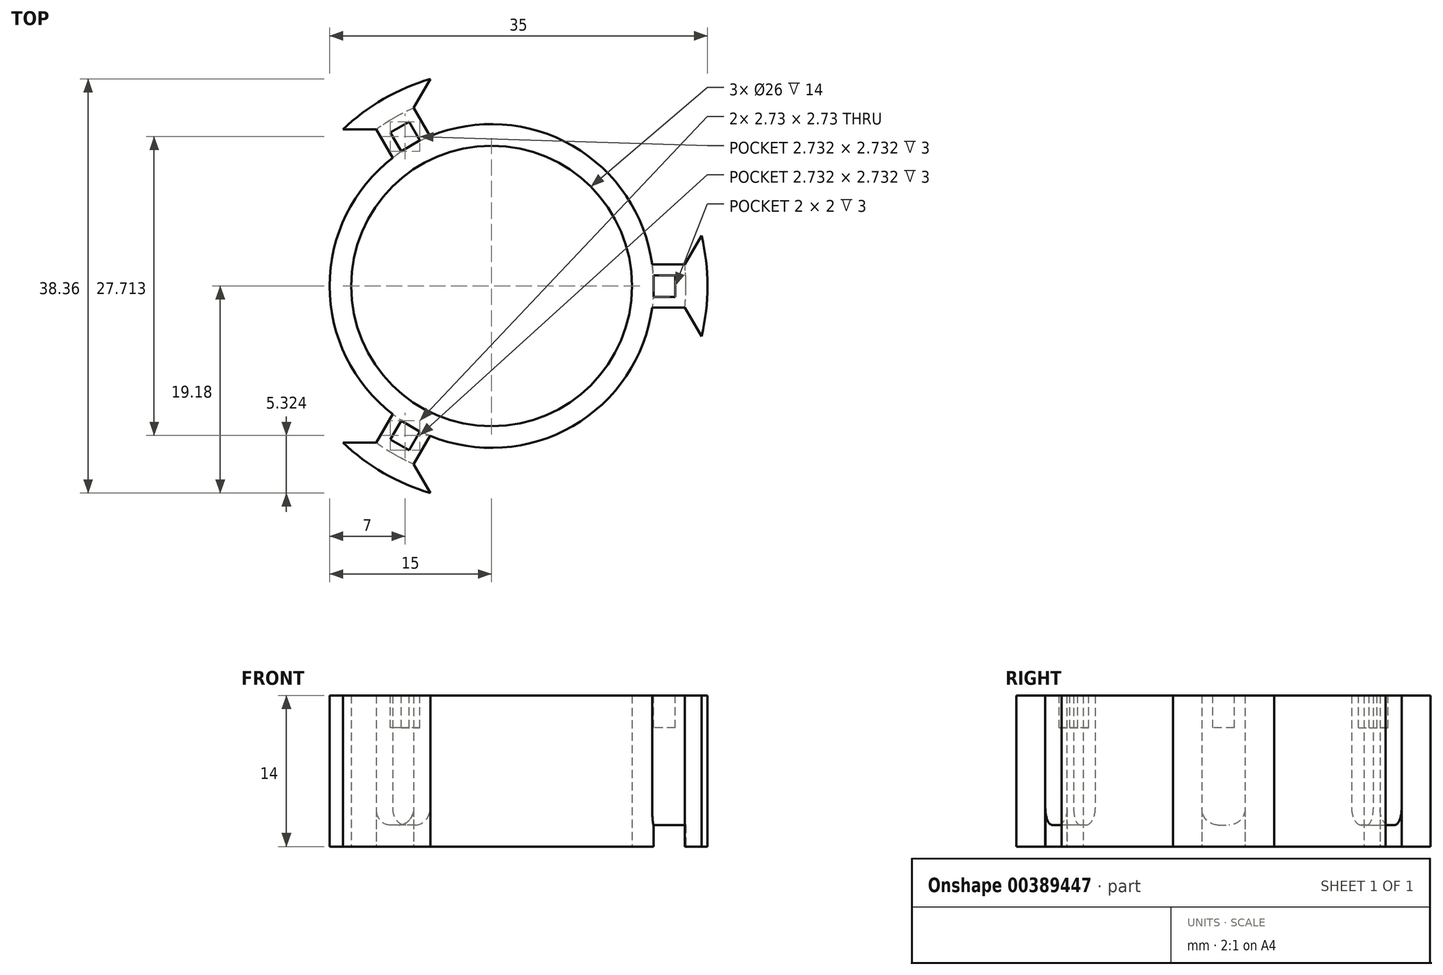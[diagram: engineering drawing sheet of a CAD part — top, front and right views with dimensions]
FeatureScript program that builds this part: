
annotation { "Feature Type Name" : "Feature", "Feature Type Description" : "" }
export const myFeature = defineFeature(function(context is Context, id is Id, definition is map)
    precondition{}
    {
        {
            var Q0;
            Q0=qCreatedBy(makeId("Top.planeOp"),FACE);
            var sketch = newSketch(context, id + "F0", { "sketchPlane" : qUnion([Q0])});
            skCircle(sketch, "E0", {"center": v(0, 0) * mm, "radius": 13 * mm});
            skCircle(sketch, "E1", {"center": v(0, 0) * mm, "radius": 15 * mm});
            skPoint(sketch, "E2.end.orphan", {"position": v(0, 21.28) * mm});
            skLineSegment(sketch, "E3", {"start": v(0, 0) * mm, "end": v(20, 0) * mm});
            skLineSegment(sketch, "E4", {"start": v(20, 0) * mm, "end": v(0, 0) * mm});
            skLineSegment(sketch, "E5", {"start": v(-10, -17.32) * mm, "end": v(0, 0) * mm});
            skLineSegment(sketch, "E6", {"start": v(0, 0) * mm, "end": v(-10, 17.32) * mm});
            skLineSegment(sketch, "E7", {"start": v(-9.17, 11.87) * mm, "end": v(-11.68, 16.23) * mm});
            skLineSegment(sketch, "E8", {"start": v(-5.7, 13.87) * mm, "end": v(-8.21, 18.22) * mm});
            skLineSegment(sketch, "E9", {"start": v(-11.73, 16.32) * mm, "end": v(-11.74, 16.31) * mm});
            skArc(sketch, "E10", {"start": v(-5.67, 19.18) * mm, "mid": v(-10, 17.32) * mm, "end": v(-13.77, 14.5) * mm});
            skLineSegment(sketch, "E11", {"start": v(-10.68, 14.5) * mm, "end": v(-13.77, 14.5) * mm});
            skLineSegment(sketch, "E12", {"start": v(-5.67, 19.18) * mm, "end": v(-7.22, 16.5) * mm});
            skPoint(sketch, "E13.orphan", {"position": v(-8.22, 18.23) * mm});
            skLineSegment(sketch, "E14.1.0", {"start": v(-9.17, -11.87) * mm, "end": v(-11.68, -16.22) * mm});
            skLineSegment(sketch, "E14.1.1", {"start": v(-13.77, -14.5) * mm, "end": v(-10.68, -14.5) * mm});
            skArc(sketch, "E14.1.2", {"start": v(-13.77, -14.5) * mm, "mid": v(-10, -17.32) * mm, "end": v(-5.67, -19.18) * mm});
            skLineSegment(sketch, "E14.1.3", {"start": v(-7.22, -16.5) * mm, "end": v(-5.67, -19.18) * mm});
            skLineSegment(sketch, "E14.1.4", {"start": v(-5.7, -13.87) * mm, "end": v(-8.22, -18.23) * mm});
            skLineSegment(sketch, "E14.2.0", {"start": v(14.87, -2) * mm, "end": v(19.89, -2) * mm});
            skLineSegment(sketch, "E14.2.1", {"start": v(19.45, -4.68) * mm, "end": v(17.9, -2) * mm});
            skArc(sketch, "E14.2.2", {"start": v(19.45, -4.68) * mm, "mid": v(20, 0) * mm, "end": v(19.45, 4.68) * mm});
            skLineSegment(sketch, "E14.2.3", {"start": v(17.9, 2) * mm, "end": v(19.45, 4.68) * mm});
            skLineSegment(sketch, "E14.2.4", {"start": v(14.87, 2) * mm, "end": v(19.9, 2) * mm});
            skSolve(sketch);
        }
        {
            var Q0;
            Q0=qSketchRegion(id+"F0",true);
            extrude(context, id + "F1", {"entities" : qUnion([Q0]), "depth" : 28 * mm});
        }
        {
            var Q0;
            Q0=qCreatedBy(makeId("Top.planeOp"),FACE);
            var sketch = newSketch(context, id + "F2", { "sketchPlane" : qUnion([Q0])});
            skCircle(sketch, "E15", {"center": v(0, 0) * mm, "radius": 15 * mm});
            skCircle(sketch, "E16", {"center": v(0, 0) * mm, "radius": 18 * mm});
            skSolve(sketch);
        }
        {
            var Q0;
            Q0=makeQuery(id+"F2.imprint","IMPRINT",FACE,{"disambiguationData":[TD([[makeQuery(id+"F2.imprint","IMPRINT",EDGE,{"derivedFrom":sQuery(id+"F2.wireOp",EDGE,"E15")}),-1.0]])]});
            extrude(context, id + "F3", {"entities" : qUnion([Q0]), "operationType" : NewBodyOperationType.REMOVE, "depth" : 2 * mm});
        }
        {
            var Q0;
            Q0=makeQuery(id+"F1.opExtrude","CAP_FACE",FACE,{"disambiguationData":[OSD([sQuery(id+"F0.wireOp",EDGE,"E0"),sQuery(id+"F0.wireOp",EDGE,"E1"),sQuery(id+"F0.wireOp",EDGE,"E7"),sQuery(id+"F0.wireOp",EDGE,"E8"),sQuery(id+"F0.wireOp",EDGE,"E10"),sQuery(id+"F0.wireOp",EDGE,"E11"),sQuery(id+"F0.wireOp",EDGE,"E12"),sQuery(id+"F0.wireOp",EDGE,"E14.1.0"),sQuery(id+"F0.wireOp",EDGE,"E14.1.1"),sQuery(id+"F0.wireOp",EDGE,"E14.1.2"),sQuery(id+"F0.wireOp",EDGE,"E14.1.3"),sQuery(id+"F0.wireOp",EDGE,"E14.1.4"),sQuery(id+"F0.wireOp",EDGE,"E14.2.0"),sQuery(id+"F0.wireOp",EDGE,"E14.2.1"),sQuery(id+"F0.wireOp",EDGE,"E14.2.2"),sQuery(id+"F0.wireOp",EDGE,"E14.2.3"),sQuery(id+"F0.wireOp",EDGE,"E14.2.4")])],"isStart":false});
            var sketch = newSketch(context, id + "F4", { "sketchPlane" : qUnion([Q0])});
            skCircle(sketch, "E17", {"center": v(0, 0) * mm, "radius": 15 * mm});
            skCircle(sketch, "E18", {"center": v(0, 0) * mm, "radius": 18.01 * mm});
            skSolve(sketch);
        }
        {
            var Q0;
            Q0=qSketchRegion(id+"F4",true);
            extrude(context, id + "F5", {"entities" : qUnion([Q0]), "operationType" : NewBodyOperationType.REMOVE, "oppositeDirection" : true, "depth" : 2 * mm});
        }
        {
            var Q0;
            Q0=makeQuery(id+"F5.boolean.opBoolean","INTERSECT",EDGE,{"derivedFrom":[makeQuery(id+"F1.opExtrude","SWEPT_FACE",FACE,{"disambiguationData":[OSD([sQuery(id+"F0.wireOp",EDGE,"E14.1.4")])]}),makeQuery(id+"F5.opExtrude","CAP_FACE",FACE,{"disambiguationData":[OSD([sQuery(id+"F4.wireOp",EDGE,"E17"),sQuery(id+"F4.wireOp",EDGE,"E18")])],"isStart":false})]});
            var Q1;
            Q1=makeQuery(id+"F5.boolean.opBoolean","INTERSECT",EDGE,{"derivedFrom":[makeQuery(id+"F1.opExtrude","SWEPT_FACE",FACE,{"disambiguationData":[OSD([sQuery(id+"F0.wireOp",EDGE,"E14.1.0")])]}),makeQuery(id+"F5.opExtrude","CAP_FACE",FACE,{"disambiguationData":[OSD([sQuery(id+"F4.wireOp",EDGE,"E17"),sQuery(id+"F4.wireOp",EDGE,"E18")])],"isStart":false})]});
            var Q2;
            Q2=makeQuery(id+"F5.boolean.opBoolean","INTERSECT",EDGE,{"derivedFrom":[makeQuery(id+"F1.opExtrude","SWEPT_FACE",FACE,{"disambiguationData":[OSD([sQuery(id+"F0.wireOp",EDGE,"E14.2.0")])]}),makeQuery(id+"F5.opExtrude","CAP_FACE",FACE,{"disambiguationData":[OSD([sQuery(id+"F4.wireOp",EDGE,"E17"),sQuery(id+"F4.wireOp",EDGE,"E18")])],"isStart":false})]});
            var Q3;
            Q3=makeQuery(id+"F5.boolean.opBoolean","INTERSECT",EDGE,{"derivedFrom":[makeQuery(id+"F1.opExtrude","SWEPT_FACE",FACE,{"disambiguationData":[OSD([sQuery(id+"F0.wireOp",EDGE,"E14.2.4")])]}),makeQuery(id+"F5.opExtrude","CAP_FACE",FACE,{"disambiguationData":[OSD([sQuery(id+"F4.wireOp",EDGE,"E17"),sQuery(id+"F4.wireOp",EDGE,"E18")])],"isStart":false})]});
            var Q4;
            Q4=makeQuery(id+"F5.boolean.opBoolean","INTERSECT",EDGE,{"derivedFrom":[makeQuery(id+"F1.opExtrude","SWEPT_FACE",FACE,{"disambiguationData":[OSD([sQuery(id+"F0.wireOp",EDGE,"E8")])]}),makeQuery(id+"F5.opExtrude","CAP_FACE",FACE,{"disambiguationData":[OSD([sQuery(id+"F4.wireOp",EDGE,"E17"),sQuery(id+"F4.wireOp",EDGE,"E18")])],"isStart":false})]});
            var Q5;
            Q5=makeQuery(id+"F5.boolean.opBoolean","INTERSECT",EDGE,{"derivedFrom":[makeQuery(id+"F1.opExtrude","SWEPT_FACE",FACE,{"disambiguationData":[OSD([sQuery(id+"F0.wireOp",EDGE,"E7")])]}),makeQuery(id+"F5.opExtrude","CAP_FACE",FACE,{"disambiguationData":[OSD([sQuery(id+"F4.wireOp",EDGE,"E17"),sQuery(id+"F4.wireOp",EDGE,"E18")])],"isStart":false})]});
            var Q6;
            Q6=makeQuery(id+"F3.boolean.opBoolean","INTERSECT",EDGE,{"derivedFrom":[makeQuery(id+"F1.opExtrude","SWEPT_FACE",FACE,{"disambiguationData":[OSD([sQuery(id+"F0.wireOp",EDGE,"E7")])]}),makeQuery(id+"F3.opExtrude","CAP_FACE",FACE,{"disambiguationData":[OSD([sQuery(id+"F2.wireOp",EDGE,"E15"),sQuery(id+"F2.wireOp",EDGE,"E16")])],"isStart":false})]});
            var Q7;
            Q7=makeQuery(id+"F3.boolean.opBoolean","INTERSECT",EDGE,{"derivedFrom":[makeQuery(id+"F1.opExtrude","SWEPT_FACE",FACE,{"disambiguationData":[OSD([sQuery(id+"F0.wireOp",EDGE,"E8")])]}),makeQuery(id+"F3.opExtrude","CAP_FACE",FACE,{"disambiguationData":[OSD([sQuery(id+"F2.wireOp",EDGE,"E15"),sQuery(id+"F2.wireOp",EDGE,"E16")])],"isStart":false})]});
            var Q8;
            Q8=makeQuery(id+"F3.boolean.opBoolean","INTERSECT",EDGE,{"derivedFrom":[makeQuery(id+"F1.opExtrude","SWEPT_FACE",FACE,{"disambiguationData":[OSD([sQuery(id+"F0.wireOp",EDGE,"E14.2.4")])]}),makeQuery(id+"F3.opExtrude","CAP_FACE",FACE,{"disambiguationData":[OSD([sQuery(id+"F2.wireOp",EDGE,"E15"),sQuery(id+"F2.wireOp",EDGE,"E16")])],"isStart":false})]});
            var Q9;
            Q9=makeQuery(id+"F3.boolean.opBoolean","INTERSECT",EDGE,{"derivedFrom":[makeQuery(id+"F1.opExtrude","SWEPT_FACE",FACE,{"disambiguationData":[OSD([sQuery(id+"F0.wireOp",EDGE,"E14.2.0")])]}),makeQuery(id+"F3.opExtrude","CAP_FACE",FACE,{"disambiguationData":[OSD([sQuery(id+"F2.wireOp",EDGE,"E15"),sQuery(id+"F2.wireOp",EDGE,"E16")])],"isStart":false})]});
            var Q10;
            Q10=makeQuery(id+"F3.boolean.opBoolean","INTERSECT",EDGE,{"derivedFrom":[makeQuery(id+"F1.opExtrude","SWEPT_FACE",FACE,{"disambiguationData":[OSD([sQuery(id+"F0.wireOp",EDGE,"E14.1.0")])]}),makeQuery(id+"F3.opExtrude","CAP_FACE",FACE,{"disambiguationData":[OSD([sQuery(id+"F2.wireOp",EDGE,"E15"),sQuery(id+"F2.wireOp",EDGE,"E16")])],"isStart":false})]});
            var Q11;
            Q11=makeQuery(id+"F3.boolean.opBoolean","INTERSECT",EDGE,{"derivedFrom":[makeQuery(id+"F1.opExtrude","SWEPT_FACE",FACE,{"disambiguationData":[OSD([sQuery(id+"F0.wireOp",EDGE,"E14.1.4")])]}),makeQuery(id+"F3.opExtrude","CAP_FACE",FACE,{"disambiguationData":[OSD([sQuery(id+"F2.wireOp",EDGE,"E15"),sQuery(id+"F2.wireOp",EDGE,"E16")])],"isStart":false})]});
            fillet(context, id + "F6", {"entities" : qUnion([Q0, Q1, Q2, Q3, Q4, Q5, Q6, Q7, Q8, Q9, Q10, Q11]), "radius" : 1.5 * mm, "tangentPropagation" : true, "allowEdgeOverflow" : false});
        }
        {
            var Q0;
            {var subQ0=sQuery(id+"F0.wireOp",EDGE,"E14.1.1");var subQ1=sQuery(id+"F0.wireOp",EDGE,"E14.1.2");var subQ2=sQuery(id+"F0.wireOp",EDGE,"E14.1.3");Q0=makeQuery(id+"F5.boolean.opBoolean","SPLIT",FACE,{"disambiguationData":[TD([makeQuery(id+"F1.opExtrude","SWEPT_FACE",FACE,{"disambiguationData":[OSD([subQ0])]})])],"derivedFrom":makeQuery(id+"F1.opExtrude","CAP_FACE",FACE,{"disambiguationData":[OSD([sQuery(id+"F0.wireOp",EDGE,"E0"),sQuery(id+"F0.wireOp",EDGE,"E1"),sQuery(id+"F0.wireOp",EDGE,"E7"),sQuery(id+"F0.wireOp",EDGE,"E8"),sQuery(id+"F0.wireOp",EDGE,"E10"),sQuery(id+"F0.wireOp",EDGE,"E11"),sQuery(id+"F0.wireOp",EDGE,"E12"),sQuery(id+"F0.wireOp",EDGE,"E14.1.0"),subQ0,subQ1,subQ2,sQuery(id+"F0.wireOp",EDGE,"E14.1.4"),sQuery(id+"F0.wireOp",EDGE,"E14.2.0"),sQuery(id+"F0.wireOp",EDGE,"E14.2.1"),sQuery(id+"F0.wireOp",EDGE,"E14.2.2"),sQuery(id+"F0.wireOp",EDGE,"E14.2.3"),sQuery(id+"F0.wireOp",EDGE,"E14.2.4")])],"isStart":false})});}
            var sketch = newSketch(context, id + "F7", { "sketchPlane" : qUnion([Q0])});
            skCircle(sketch, "E19", {"center": v(0, 0) * mm, "radius": 25.29 * mm});
            skSolve(sketch);
        }
        {
            var Q0;
            Q0=qSketchRegion(id+"F7",true);
            extrude(context, id + "F8", {"entities" : qUnion([Q0]), "operationType" : NewBodyOperationType.REMOVE, "oppositeDirection" : true, "depth" : (28 / 2) * mm});
        }
        {
            var Q0;
            Q0=makeQuery(id+"F8.boolean.opBoolean","COPY",FACE,{"derivedFrom":makeQuery(id+"F8.opExtrude","CAP_FACE",FACE,{"disambiguationData":[OSD([sQuery(id+"F7.wireOp",EDGE,"E19")])],"isStart":false})});
            var sketch = newSketch(context, id + "F9", { "sketchPlane" : qUnion([Q0])});
            skLineSegment(sketch, "E20.bottom", {"start": v(17, 1) * mm, "end": v(15, 1) * mm});
            skLineSegment(sketch, "E20.top", {"start": v(17, -1) * mm, "end": v(15, -1) * mm});
            skLineSegment(sketch, "E20.left", {"start": v(17, 1) * mm, "end": v(17, -1) * mm});
            skLineSegment(sketch, "E20.right", {"start": v(15, 1) * mm, "end": v(15, -1) * mm});
            skPoint(sketch, "E20.middle", {"position": v(16, 0) * mm});
            skLineSegment(sketch, "E21", {"start": v(-9.37, -14.22) * mm, "end": v(-8.37, -12.5) * mm});
            skLineSegment(sketch, "E22", {"start": v(-8.37, -12.5) * mm, "end": v(-6.63, -13.5) * mm});
            skLineSegment(sketch, "E23", {"start": v(-6.63, -13.5) * mm, "end": v(-7.63, -15.22) * mm});
            skLineSegment(sketch, "E24", {"start": v(-7.63, -15.22) * mm, "end": v(-9.37, -14.22) * mm});
            skLineSegment(sketch, "E25", {"start": v(-8.37, 12.5) * mm, "end": v(-6.63, 13.5) * mm});
            skLineSegment(sketch, "E26", {"start": v(-6.63, 13.5) * mm, "end": v(-7.63, 15.22) * mm});
            skLineSegment(sketch, "E27", {"start": v(-7.63, 15.22) * mm, "end": v(-9.37, 14.22) * mm});
            skLineSegment(sketch, "E28", {"start": v(-8.37, 12.5) * mm, "end": v(-9.37, 14.22) * mm});
            skSolve(sketch);
        }
        {
            var Q0;
            Q0=qSketchRegion(id+"F9",true);
            extrude(context, id + "F10", {"entities" : qUnion([Q0]), "operationType" : NewBodyOperationType.REMOVE, "oppositeDirection" : true, "depth" : 3 * mm});
        }
    });
